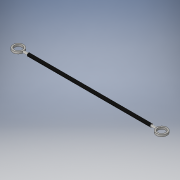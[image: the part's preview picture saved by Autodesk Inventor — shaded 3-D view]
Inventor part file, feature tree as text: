
AUTODESK INVENTOR PART (.ipt)
format: ipt  version: 2016 (Build 200138000, 138)  size: 114,176 bytes
history: native  units: in
note: dims shown in document units (in); Inventor stores cm internally (conversion verified against a paired STEP export)
features: other x4, sketch x3
ambient origin geometry x8: Origin, YZ Plane, XZ Plane, XY Plane, X Axis, Y Axis, Z Axis, Center Point
bodies: Solid1 (feature_tree)
feature tree (7):
  other  "Tie Rod.ipt"
  other  "Solid1::Tie Rod.ipt"
  other  "TaggingFeature1"
  sketch  "Sketch1"  dims[d0=0.3937in]
  sketch  "Sketch3"
  sketch  "Sketch4"
  other  "Mid Plane"
